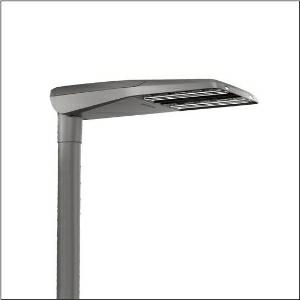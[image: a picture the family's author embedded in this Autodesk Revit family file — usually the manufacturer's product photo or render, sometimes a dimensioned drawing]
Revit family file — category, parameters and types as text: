
# Revit family: streetlight_sl_11_iq_midi___st1_2a_5xc3a51e08le_ac55
name_source: partatom
category: Lighting Fixtures
units: mm (PartAtom-declared; Revit-internal decimal feet)

## family parameters
Cut with Voids When Loaded = No
Host = Face
Light Source = No
Part Type = Normal
Room Calculation Point = No
Round Connector Dimension = Use Diameter
Shared = No

## types (1)
- --- (1 x LED, 9210 lm, 60.4 W, 3000K)
    Apparent Load = 60 VA
    CIE Flux Codes = 32 70 96 100 100
    Color Rendering = 70
    Color Temperature = 3000K
    Default Elevation = 1800 mm
    Description = Streetlight SL 11 iQ midi, mast luminaire, primary light control with 3 zone facetted reflector, of plastic, silver coated, highly specular, primary optical cover: cover, of PMMA, transparent, light distribution: ST1.2a, light emission: direct distribution, primary light characteristic: asymmetric, installation type: post-top, side-entry, lamps: LED, High Power LED, rated values: 9.210lm | 60,4W | 152,5lm/W (begin service life); end service life: 9.210lm | 62,5W; at 50% lumin. flux: 4.605lm | 29,6W | 155,6lm/W, colour temperature: 3000K, colour rendering: CRI > 70, light colour: 730, light setting 1 begin service life: 100% | 9.210lm | 60,4W | 152,5lm/W | 3.000K, light setting 1 end service life: 62,5W, further light settings possible, control: optimised constant luminous flux control (CLO 2.0), Desk-Remote (wireless, voltage-free reading and setting of iQ features in the workshop via application-optimized NFC function/RFID function), Light-Fading, Smart-Wire, Night-Set, Lumen-Switch, Temp-Guard, Auto-Match, with cable H07RN-F 3x 1.5mm², mains connection: 230..240V, AC, 50/60Hz, connection cable pre-assembled, cable length: 8,5m, luminaire housing, of diecast aluminium, powder-coated, SITECO metallic grey (DB 702S), please order mast flange separately, inclination adjustable without tools: 0°, 5°, 10°, 15° (post-top) | 0°, -5°, -10°, -15° (side-entry), sealing non-destructively replaceable, multi-level sealing system, length: 780mm, width: 376mm, height: 118mm, mast flange for spigot size: 42mm (side-entry): 5XC10008XM4, 60/48mm (side-entry/post-top): 5XC10108XM2, 76/60mm (side-entry/post-top): 5XC10108XM1, equipment: standard, protection rating (complete): IP66, insulation class (complete): insulation class II (safety insulation), certification: CE, ENEC, ENEC+, VDE, impact resistance: IK10, permissible operating ambient temperature for outdoor applications: -25..+50°C, standard-compliant lighting for roads and squares, Environmental Product Declaration (EPD) tested and certified by an independent institute, packaging unit: 1 piece

Light Distribution: ST1.2a
    Height = 118 mm
    Lamp = 1 x LED
    Lamp Light Flux = 9210 lm
    Lamp Power = 60.4 W
    Lamp count = 1
    Length = 780 mm
    Luminous efficacy = 152 lm/W
    Manufacturer = Siteco
    ModVariant = No
    Model = 5XC3A51E08LE
    Number of Poles = 1
    OnlyDefault = Yes
    Power Factor = 1
    Product Name = Streetlight SL 11 iQ midi | ST1.2a
    Product group = mast luminaire | pylon top
    ProductGroupID = 6100
    Protection Class = Protection class II
    Protection Degree = IP 66
    RLX_Detail_Level = 1
    RLX_Emergency_Light_Flux = 0 lm
    RLX_Emergency_Type = 0
    RLX_Emergency_Type_DB = No
    RlxData = <blob elided: 70757 chars, md5=7e2809d0>
    Socket = socket
    Standby Power = 0 W
    System Light Flux = 9210 lm
    System Power = 60 W
    Type Comments = factory setting: luminous flux: 100 % | dim-lin: 254 | 520 mA
    Type Image = l_1005960.jpg
    URL = http://relux.com
    VarID = @adj_194445
    Voltage = 0 V
    Weight = 0.00 kg
    Width = 376 mm

## geometry (parser evidence)
native form markers: Blend x4, Sweep x10
no freeform markers — native parametric forms only
